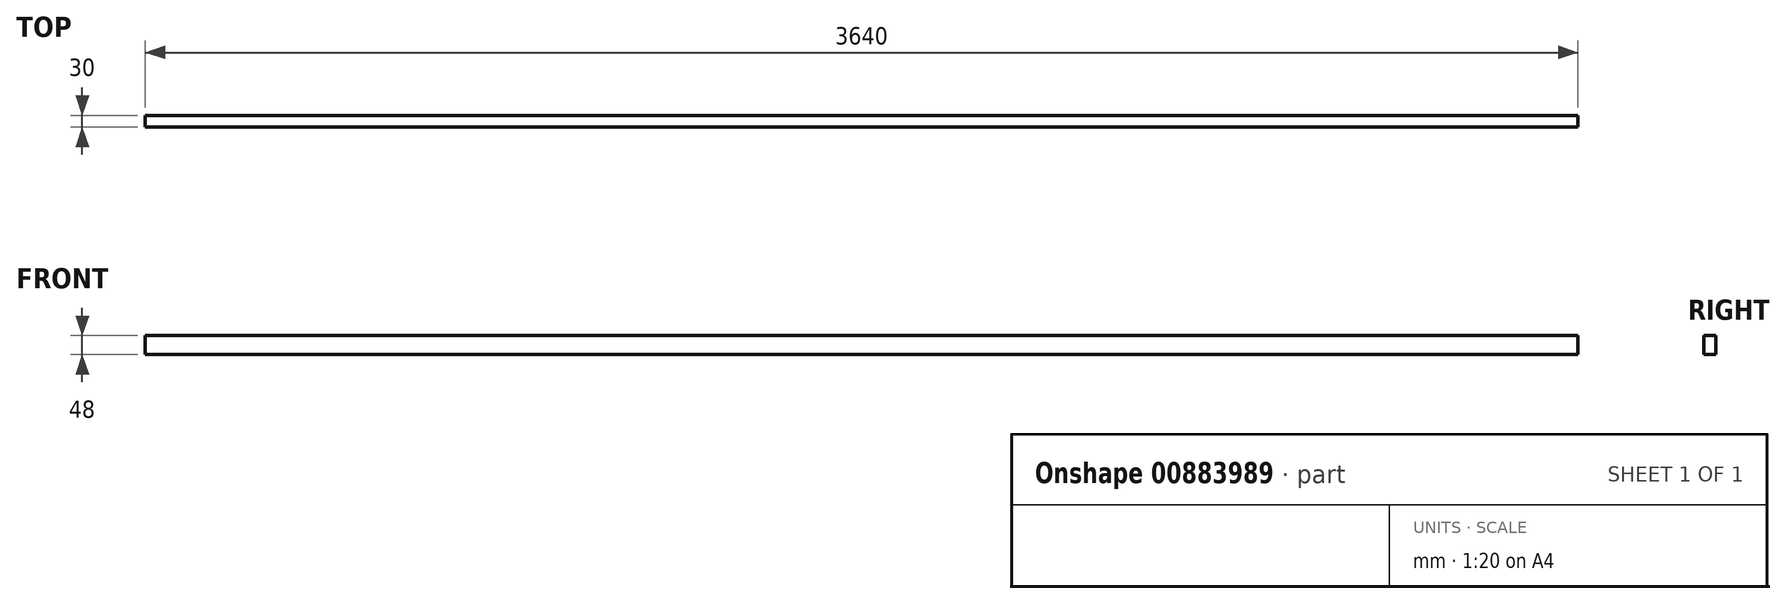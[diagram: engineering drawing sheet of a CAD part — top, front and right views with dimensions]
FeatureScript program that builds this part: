
annotation { "Feature Type Name" : "Feature", "Feature Type Description" : "" }
export const myFeature = defineFeature(function(context is Context, id is Id, definition is map)
    precondition{}
    {
        {
            var Q0;
            Q0=qCreatedBy(makeId("Top.planeOp"),FACE);
            var sketch = newSketch(context, id + "F0", { "sketchPlane" : qUnion([Q0])});
            skLineSegment(sketch, "E0.bottom", {"start": v(1820, -15) * mm, "end": v(-1820, -15) * mm});
            skLineSegment(sketch, "E0.top", {"start": v(1820, 15) * mm, "end": v(-1820, 15) * mm});
            skLineSegment(sketch, "E0.left", {"start": v(1820, -15) * mm, "end": v(1820, 15) * mm});
            skLineSegment(sketch, "E0.right", {"start": v(-1820, -15) * mm, "end": v(-1820, 15) * mm});
            skPoint(sketch, "E0.middle", {"position": v(0, 0) * mm});
            skSolve(sketch);
        }
        {
            var Q0;
            Q0=makeQuery(id+"F0.imprint","IMPRINT",FACE,{"disambiguationData":[TD([[makeQuery(id+"F0.imprint","IMPRINT",EDGE,{"derivedFrom":sQuery(id+"F0.wireOp",EDGE,"E0.bottom")}),-1.0]])]});
            extrude(context, id + "F1", {"entities" : qUnion([Q0]), "oppositeDirection" : true, "depth" : 48 * mm, "offsetDistance" : 25 * mm});
        }
    });
